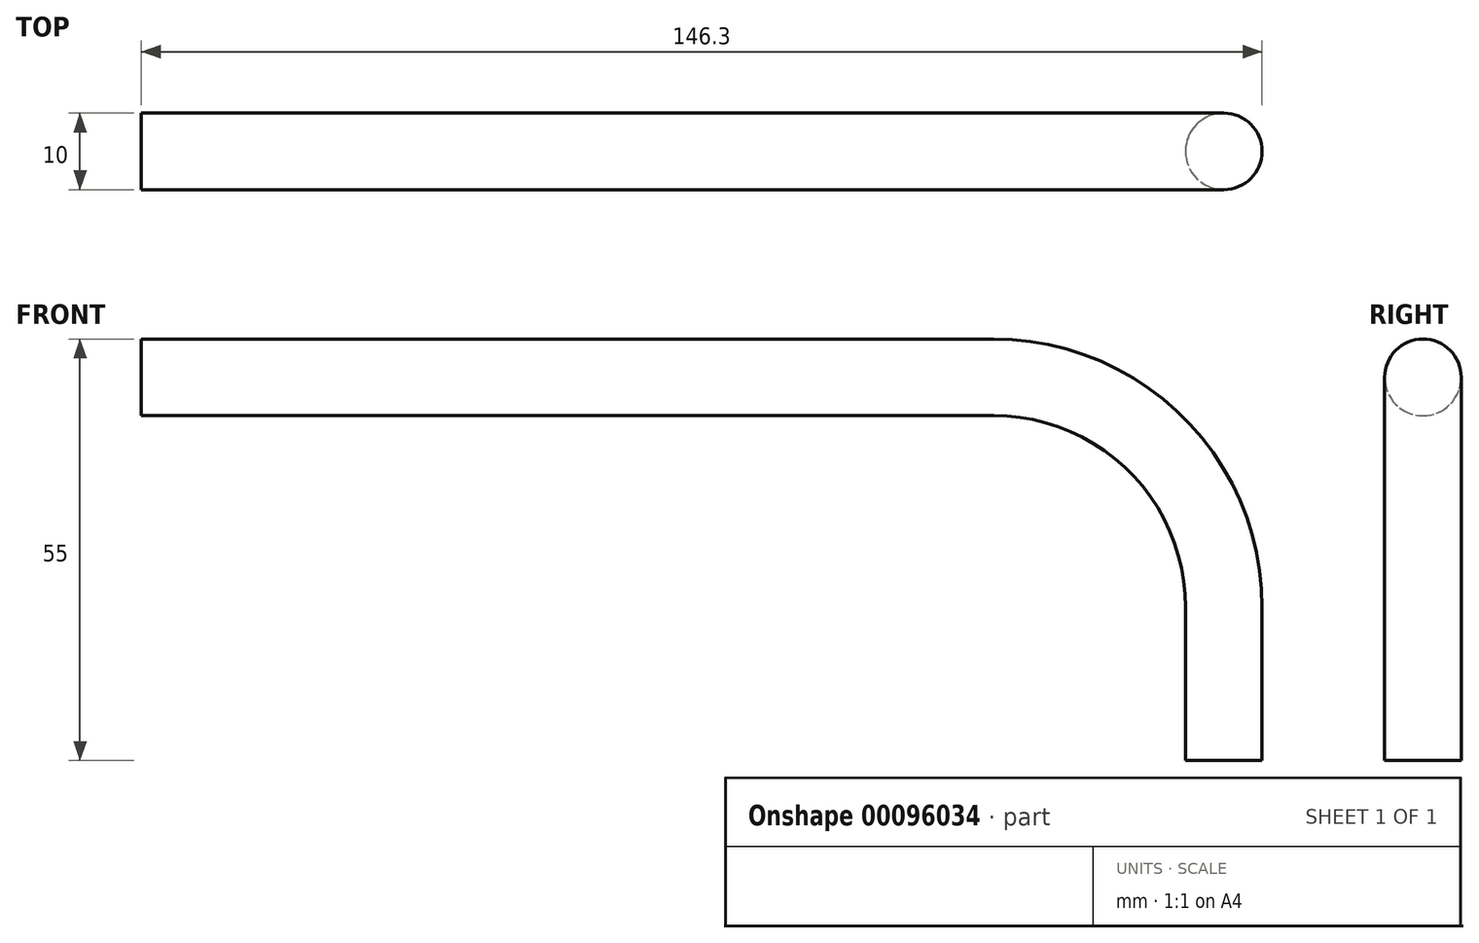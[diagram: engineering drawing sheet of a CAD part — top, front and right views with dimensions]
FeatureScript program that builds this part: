
annotation { "Feature Type Name" : "Feature", "Feature Type Description" : "" }
export const myFeature = defineFeature(function(context is Context, id is Id, definition is map)
    precondition{}
    {
        {
            var Q0;
            Q0=qCreatedBy(makeId("Front.planeOp"),FACE);
            var sketch = newSketch(context, id + "F0", { "sketchPlane" : qUnion([Q0])});
            skLineSegment(sketch, "E0", {"start": v(0, 0) * mm, "end": v(111.3, 0) * mm});
            skLineSegment(sketch, "E1", {"start": v(141.3, -30) * mm, "end": v(141.3, -50) * mm});
            skArc(sketch, "E2.filletArc", {"start": v(141.3, -30) * mm, "mid": v(132.51, -8.79) * mm, "end": v(111.3, 0) * mm});
            skSolve(sketch);
        }
        {
            var Q0;
            Q0=qCreatedBy(makeId("Right.planeOp"),FACE);
            var sketch = newSketch(context, id + "F1", { "sketchPlane" : qUnion([Q0])});
            skCircle(sketch, "E3", {"center": v(0, 0) * mm, "radius": 5 * mm});
            skSolve(sketch);
        }
        {
            var Q0;
            Q0 = qSketchRegion(id + "F1", true);
            var Q1;
            Q1 = qConstructionFilter(qBodyType(qCreatedBy(id + "F0" ,EDGE), BodyType.WIRE), ConstructionObject.NO);
            sweep(context, id + "F2", {"profiles" : qUnion([Q0]), "path" : qUnion([Q1])});
        }
    });
